# Revit family: HVAC_HeatPumpAW_Enertech_CTC-EcoAir-510M
name_source: partatom
category: Specialty Equipment
units: mm (PartAtom-declared; Revit-internal decimal feet)

## family parameters
Always vertical = Yes
Cut with Voids When Loaded = No
OmniClass Number = 23.75.00.00
OmniClass Title = Climate Control (HVAC)
Part Type = Normal
Room Calculation Point = No
Round Connector Dimension = Use Diameter
Shared = No
Work Plane-Based = No

## types (1)
- CTC EcoAir 510M  230V1N
    AirFlow max (m3/h) = 3800
    AirFlow nominal (m3/h) = 0
    AssetType = Fixed
    BIMObjectName = HVAC_HeatPumpAW_Enertech_CTC-EcoAir-510M
    Brand = CTC
    BrineSystem_Min_MaxPressure = 0-31
    CO2Equivalent = 4.594
    COP max: W35 & A +12 = 0
    COP max: W35 & A +2 = 0.5
    COP max: W35 & A +7 = 0.45
    COP max: W35 & A -15 = 0
    COP max: W35 & A -7 = 0.55
    COP min: W35 & A +12 = 0
    COP min: W35 & A +2 = 5.00
    COP min: W35 & A +7 = 6.67
    COP min: W35 & A -15 = 0
    COP min: W35 & A -7 = 2.73
    Capacity = Variable
    Category = Heat Pumps, Air-to-water
    Color = grey
    CoolingCapacity max: A35 & W18 = 6000 W
    CoolingCapacity max: A35 & W7 = 6000 W
    CoolingCapacity min: A35 & W18 = 8000 W
    CoolingCapacity min: A35 & W7 = 8000 W
    CoolingCapacity nominal: A35 & W18 = 4000 W
    CoolingCapacity nominal: A35 & W7 = 8000 W
    Cost = 0 $
    Default Elevation = 0 mm  [stored 0 ft]
    Description = CTC EcoAir 510M a speed controlled air-to-water heat pump,  which automatically adapts to the building's power demand during the year.
    DurationUnit = Year
    EANNumber = 7333077090944
    EER max: A35 & W18 = 0
    EER max: A35 & W7 = 0
    EER min: A35 & W18 = 0
    EER min: A35 & W7 = 0
    EER nominal: A35 & W18 = 0
    EER nominal: A35 & W7 = 0
    ElectricalDeviceNominalPower = 0 W
    EnergyClassHeatingWithControl W35 = A+++
    EnergyClassHeatingWithControl W55 = A++
    EnergyClassHeatingWithoutControl W35 = A++
    EnergyClassHeatingWithoutControl W55 = A++
    GroupFuse = 25
    HasProtectiveEarth = Yes
    IP_Code = IP X4
    IfcExportAs = IfcElectricalDeviceCommon
    IfcExportType = HEATER
    InPutPower max: W35 & A +12 = 0 W
    InPutPower max: W35 & A +2 = 2900 W
    InPutPower max: W35 & A +7 = 3440 W
    InPutPower max: W35 & A -15 = 1960 W
    InPutPower max: W35 & A -7 = 2170 W
    InPutPower min: W35 & A +12 = 0 W
    InPutPower min: W35 & A +2 = 2500 W
    InPutPower min: W35 & A +7 = 3000 W
    InPutPower min: W35 & A -15 = 0 W
    InPutPower min: W35 & A -7 = 1500 W
    KvsValueProduct = 5.5
    Manufacturer = CTC AB
    ManufacturerCountry = Sweden
    ManufacturerName = CTC AB
    ManufacturerURL = https://ctc.se
    Material = Steel
    MaxOperatingPressureThermalStore = 3
    MaxStartingCurrent = 2.8
    Model = CTC EcoAir 510M
    ModelNumber = 587601001
    NBSDescription = Air to water heat pumps
    NBSReference = 90-40-40/320
    Name = CTC-EcoAir-510M
    NominalCurrent = 0 A
    NominalDepth = 545 mm
    NominalFrequencyRange = 50 Hz
    NominalHeight = 1080 mm  [stored 3.54331 ft]
    NominalVoltage = 230 V
    NominalWidth = 1245 mm
    NumberOfPoles = 1
    PhaseAngle = 0.00°
    PowerFactor = 0 W
    ProductInformation = CTC EcoAir 510M a speed controlled air-to-water heat pump,  which automatically adapts to the building's power demand during the year.
    PumpMainMaterial = Steel - Grey
    RatedCurrent = 21 A
    RatedHeatOutputCold Pdesigh W35 = 0 W
    RatedHeatOutputCold Pdesigh W55 = 0 W
    RatedHeatOutputModerate Pdesigh W35 = 0 W
    RatedHeatOutputModerate Pdesigh W55 = 0 W
    RatedHeatOutputWarm Pdesigh W35 = 0 W
    RatedHeatOutputWarm Pdesigh W55 = 0 W
    RatedVoltage = 230 V
    RefrigerantQuantity = 2.2
    RefrigerantType = R410A
    Revision = 6
    SCOPCold W35 = 3.9
    SCOPCold W55 = 3.9
    SCOPModerate W35 = 4.4
    SCOPModerate W55 = 4.4
    SCOPWarm W35 = 5.5
    SCOPWarm W55 = 5.5
    Shape = Rectangular
    Size = 545x1245x1080
    Sound pressureLPA 10m = 33
    Sound pressureLPA 5m = 39
    SoundPowerLWA = 58
    SpecifiedOutput max: W35 & A +12 = 0 W
    SpecifiedOutput max: W35 & A +2 = 9000 W
    SpecifiedOutput max: W35 & A +7 = 11000 W
    SpecifiedOutput max: W35 & A -15 = 5500 W
    SpecifiedOutput max: W35 & A -7 = 6500 W
    SpecifiedOutput min: W35 & A +12 = 0 W
    SpecifiedOutput min: W35 & A +2 = 3100 W
    SpecifiedOutput min: W35 & A +7 = 3200 W
    SpecifiedOutput min: W35 & A -15 = 2800 W
    SpecifiedOutput min: W35 & A -7 = 3000 W
    Touchscreen = no
    UNSPSCCode = 40101806
    URL = https://ctc-heating.com
    Uniclass2 = Pr_40_70_65
    Uniclass2015Description = Preparation catering equipment
    Uniclass2015Reference = Pr_40_70_65
    UsageCurrent = 0 A
    Version = 6
    VersionDate = 13/05/2024
    WarrantyDurationUnit = Year
    WaterVolumeHeathingSystem = 2.13
    Weight = 136

note: [stored X ft] marks values corroborated as IEEE doubles in the binary element streams (Revit-internal decimal feet)

## geometry (parser evidence)
native form markers: Sweep x5
no freeform markers — native parametric forms only
